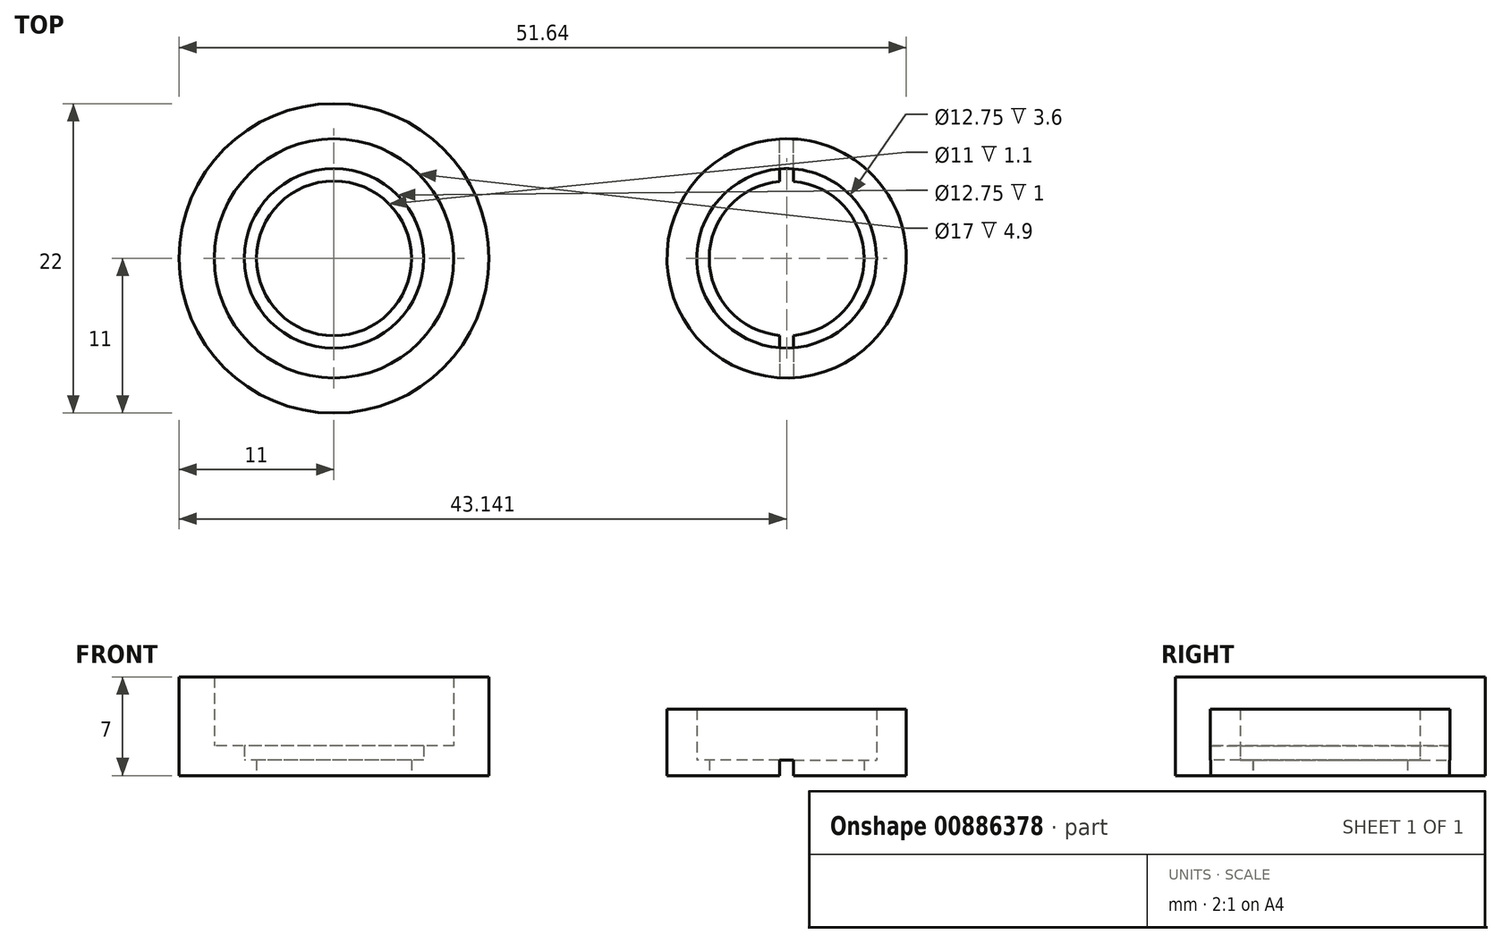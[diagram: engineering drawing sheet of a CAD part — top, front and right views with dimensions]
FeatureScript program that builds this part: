
annotation { "Feature Type Name" : "Feature", "Feature Type Description" : "" }
export const myFeature = defineFeature(function(context is Context, id is Id, definition is map)
    precondition{}
    {
        {
            var Q0;
            Q0=qCreatedBy(makeId("Top.planeOp"),FACE);
            var sketch = newSketch(context, id + "F0", { "sketchPlane" : qUnion([Q0])});
            skCircle(sketch, "E0", {"center": v(0, 0) * mm, "radius": 11 * mm});
            skCircle(sketch, "E1", {"center": v(0, 0) * mm, "radius": 5.5 * mm});
            skSolve(sketch);
        }
        {
            var Q0;
            Q0=qSketchRegion(id+"F0",true);
            extrude(context, id + "F1", {"entities" : qUnion([Q0]), "depth" : 1.1 * mm, "offsetDistance" : 25 * mm});
        }
        {
            var Q0;
            Q0=makeQuery(id+"F1.opExtrude","CAP_FACE",FACE,{"disambiguationData":[OSD([sQuery(id+"F0.wireOp",EDGE,"E0"),sQuery(id+"F0.wireOp",EDGE,"E1")])],"isStart":false});
            var sketch = newSketch(context, id + "F2", { "sketchPlane" : qUnion([Q0])});
            skCircle(sketch, "E2", {"center": v(0, 0) * mm, "radius": 6.38 * mm});
            skSolve(sketch);
        }
        {
            var Q0;
            Q0=makeQuery(id+"F2.imprint","IMPRINT",FACE,{"disambiguationData":[TD([[makeQuery(id+"F2.imprint","IMPRINT",EDGE,{"derivedFrom":sQuery(id+"F2.wireOp",EDGE,"E2")}),-1.0]])]});
            extrude(context, id + "F3", {"entities" : qUnion([Q0]), "operationType" : NewBodyOperationType.ADD, "depth" : 1 * mm, "offsetDistance" : 25 * mm});
        }
        {
            var Q0;
            Q0=makeQuery(id+"F3.opExtrude","CAP_FACE",FACE,{"disambiguationData":[OSD([sQuery(id+"F0.wireOp",EDGE,"E0"),sQuery(id+"F2.wireOp",EDGE,"E2")])],"isStart":false});
            var sketch = newSketch(context, id + "F4", { "sketchPlane" : qUnion([Q0])});
            skCircle(sketch, "E3", {"center": v(0, 0) * mm, "radius": 8.5 * mm});
            skSolve(sketch);
        }
        {
            var Q0;
            Q0=makeQuery(id+"F4.imprint","IMPRINT",FACE,{"disambiguationData":[TD([[makeQuery(id+"F4.imprint","IMPRINT",EDGE,{"derivedFrom":sQuery(id+"F4.wireOp",EDGE,"E3")}),-1.0]])]});
            extrude(context, id + "F5", {"entities" : qUnion([Q0]), "operationType" : NewBodyOperationType.ADD, "depth" : 4.9 * mm, "offsetDistance" : 25 * mm});
        }
        {
            var Q0;
            Q0=qCreatedBy(makeId("Top.planeOp"),FACE);
            var sketch = newSketch(context, id + "F6", { "sketchPlane" : qUnion([Q0])});
            skCircle(sketch, "E4", {"center": v(32.14, 0) * mm, "radius": 8.5 * mm});
            skCircle(sketch, "E5", {"center": v(32.14, 0) * mm, "radius": 5.5 * mm});
            skSolve(sketch);
        }
        {
            var Q0;
            Q0=makeQuery(id+"F6.imprint","IMPRINT",FACE,{"disambiguationData":[TD([[makeQuery(id+"F6.imprint","IMPRINT",EDGE,{"derivedFrom":sQuery(id+"F6.wireOp",EDGE,"E4")}),1.0]])]});
            extrude(context, id + "F7", {"entities" : qUnion([Q0]), "depth" : 1.1 * mm, "offsetDistance" : 25 * mm});
        }
        {
            var Q0;
            Q0=makeQuery(id+"F7.opExtrude","CAP_FACE",FACE,{"disambiguationData":[OSD([sQuery(id+"F6.wireOp",EDGE,"E4"),sQuery(id+"F6.wireOp",EDGE,"E5")])],"isStart":false});
            var sketch = newSketch(context, id + "F8", { "sketchPlane" : qUnion([Q0])});
            skCircle(sketch, "E6", {"center": v(32.14, 0) * mm, "radius": 6.38 * mm});
            skSolve(sketch);
        }
        {
            var Q0;
            Q0=makeQuery(id+"F8.imprint","IMPRINT",FACE,{"disambiguationData":[TD([[makeQuery(id+"F8.imprint","IMPRINT",EDGE,{"derivedFrom":sQuery(id+"F8.wireOp",EDGE,"E6")}),-1.0]])]});
            extrude(context, id + "F9", {"entities" : qUnion([Q0]), "operationType" : NewBodyOperationType.ADD, "depth" : 3.6 * mm, "offsetDistance" : 25 * mm});
        }
        {
            var Q0;
            Q0=makeQuery(id+"F7.opExtrude","CAP_FACE",FACE,{"disambiguationData":[OSD([sQuery(id+"F6.wireOp",EDGE,"E4"),sQuery(id+"F6.wireOp",EDGE,"E5")])],"isStart":true});
            var sketch = newSketch(context, id + "F10", { "sketchPlane" : qUnion([Q0])});
            skLineSegment(sketch, "E7", {"start": v(32.14, 0) * mm, "end": v(32.64, 0) * mm});
            skLineSegment(sketch, "E8", {"start": v(32.14, 0) * mm, "end": v(31.64, 0) * mm});
            skLineSegment(sketch, "E9", {"start": v(31.64, 0) * mm, "end": v(31.64, 8.49) * mm});
            skLineSegment(sketch, "E10", {"start": v(31.64, 0) * mm, "end": v(31.64, -8.49) * mm});
            skLineSegment(sketch, "E11", {"start": v(32.64, 0) * mm, "end": v(32.64, 8.49) * mm});
            skLineSegment(sketch, "E12", {"start": v(32.64, 0) * mm, "end": v(32.64, -8.49) * mm});
            skSolve(sketch);
        }
        {
            var Q0;
            {var subQ0=sQuery(id+"F10.wireOp",EDGE,"E9");var subQ1=makeQuery(id+"F7.opExtrude","CAP_EDGE",EDGE,{"disambiguationData":[OSD([sQuery(id+"F6.wireOp",EDGE,"E4")])],"isStart":true});var subQ2=makeQuery(id+"F10.imprint","INTERSECT",VERTEX,{"derivedFrom":[subQ1,subQ0]});Q0=makeQuery(id+"F10.imprint","IMPRINT",FACE,{"disambiguationData":[TD([[makeQuery(id+"F10.imprint","IMPRINT",EDGE,{"disambiguationData":[TD([[subQ2,1.0]])],"derivedFrom":subQ0}),-1.0]])]});}
            var Q1;
            {var subQ0=sQuery(id+"F10.wireOp",EDGE,"E10");var subQ1=makeQuery(id+"F7.opExtrude","CAP_EDGE",EDGE,{"disambiguationData":[OSD([sQuery(id+"F6.wireOp",EDGE,"E4")])],"isStart":true});var subQ2=makeQuery(id+"F10.imprint","INTERSECT",VERTEX,{"derivedFrom":[subQ1,subQ0]});Q1=makeQuery(id+"F10.imprint","IMPRINT",FACE,{"disambiguationData":[TD([[makeQuery(id+"F10.imprint","IMPRINT",EDGE,{"disambiguationData":[TD([[subQ2,1.0]])],"derivedFrom":subQ0}),1.0]])]});}
            extrude(context, id + "F11", {"entities" : qUnion([Q0, Q1]), "operationType" : NewBodyOperationType.REMOVE, "oppositeDirection" : true, "depth" : 1.1 * mm, "offsetDistance" : 25 * mm});
        }
    });
